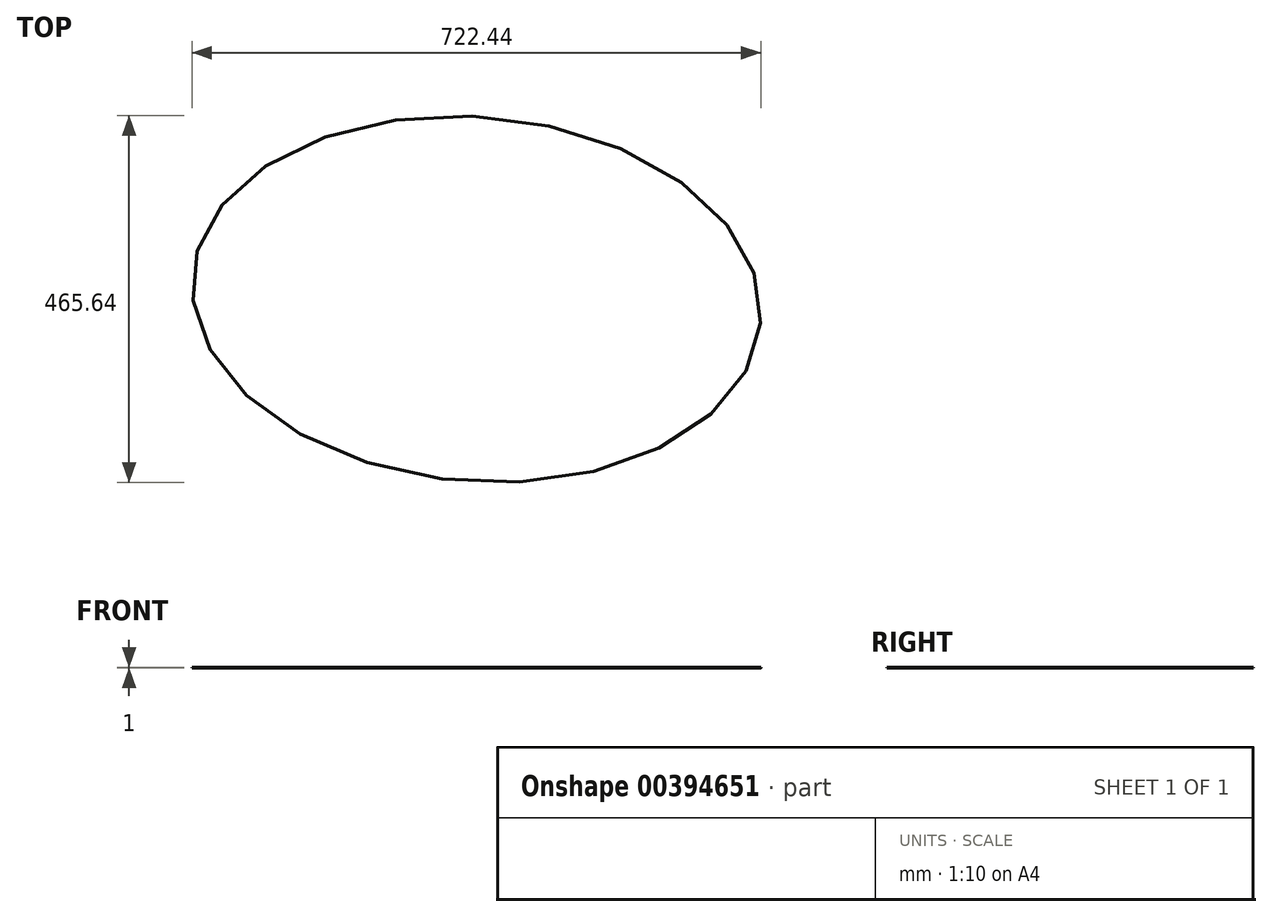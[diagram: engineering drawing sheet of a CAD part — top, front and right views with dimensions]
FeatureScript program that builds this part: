
annotation { "Feature Type Name" : "Feature", "Feature Type Description" : "" }
export const myFeature = defineFeature(function(context is Context, id is Id, definition is map)
    precondition{}
    {
        {
            var Q0;
            Q0=qCreatedBy(makeId("Top.planeOp"),FACE);
            var sketch = newSketch(context, id + "F0", { "sketchPlane" : qUnion([Q0])});
            skEllipse(sketch, "E0", {"center": v(0, 0) * mm, "majorRadius": 361.97 * mm, "minorRadius": 231.66 * mm, "majorAxis": v(1, -0.08)});
            skSolve(sketch);
        }
        {
            var Q0;
            Q0=makeQuery(id+"F0.imprint","IMPRINT",FACE,{"disambiguationData":[TD([[makeQuery(id+"F0.imprint","IMPRINT",EDGE,{"derivedFrom":sQuery(id+"F0.wireOp",EDGE,"E0")}),1.0]])]});
            extrude(context, id + "F1", {"entities" : qUnion([Q0]), "depth" : 1 * mm, "offsetDistance" : 25 * mm});
        }
    });
